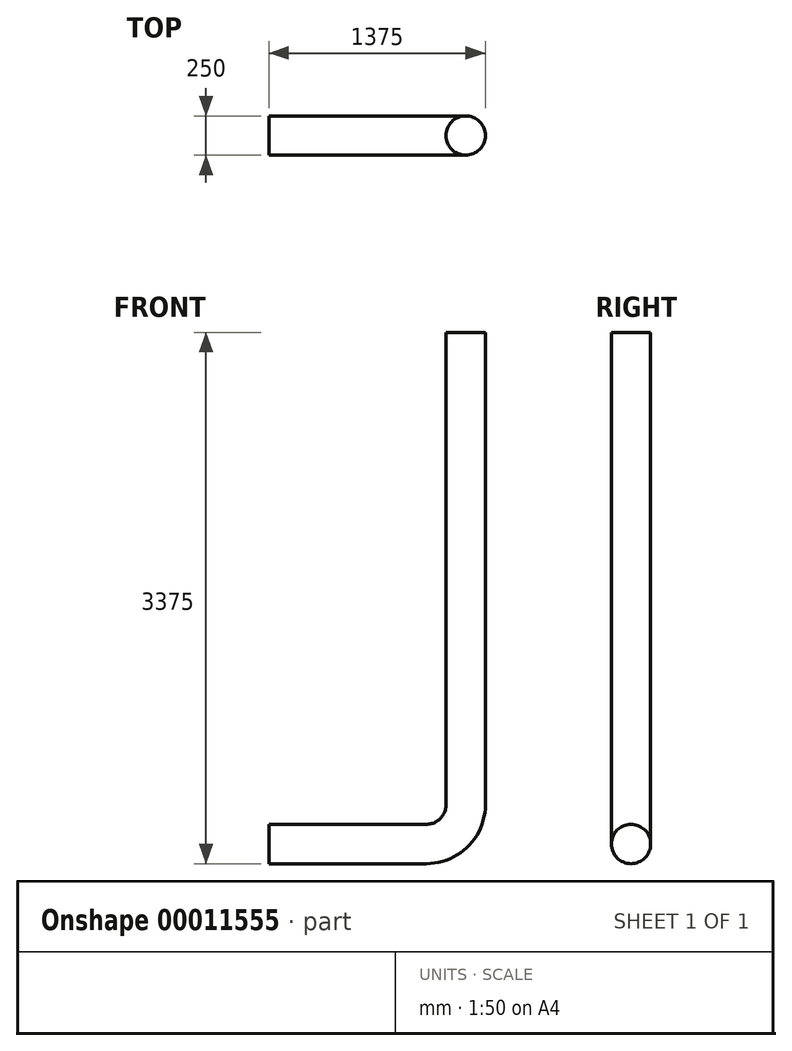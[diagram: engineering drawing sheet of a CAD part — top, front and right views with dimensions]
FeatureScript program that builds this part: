
annotation { "Feature Type Name" : "Feature", "Feature Type Description" : "" }
export const myFeature = defineFeature(function(context is Context, id is Id, definition is map)
    precondition{}
    {
        {
            var Q0;
            Q0=qCreatedBy(makeId("Right.planeOp"),FACE);
            var sketch = newSketch(context, id + "F0", { "sketchPlane" : qUnion([Q0])});
            skCircle(sketch, "E0", {"center": v(0, 0) * mm, "radius": 125 * mm});
            skSolve(sketch);
        }
        {
            var Q0;
            Q0=qCreatedBy(makeId("Front.planeOp"),FACE);
            var sketch = newSketch(context, id + "F1", { "sketchPlane" : qUnion([Q0])});
            skLineSegment(sketch, "E1", {"start": v(0, 0) * mm, "end": v(1000, 0) * mm});
            skLineSegment(sketch, "E2", {"start": v(1250, 250) * mm, "end": v(1250, 3250) * mm});
            skPoint(sketch, "E3.visualSharp", {"position": v(1250, 0) * mm});
            skArc(sketch, "E3.filletArc", {"start": v(1000, 0) * mm, "mid": v(1176.78, 73.22) * mm, "end": v(1250, 250) * mm});
            skSolve(sketch);
        }
        {
            var Q0;
            Q0 = qSketchRegion(id + "F0", true);
            var Q1;
            Q1 = qBodyType(qCreatedBy(id + "F1" ,EDGE), BodyType.WIRE);
            sweep(context, id + "F2", {"profiles" : qUnion([Q0]), "path" : qUnion([Q1])});
        }
    });
